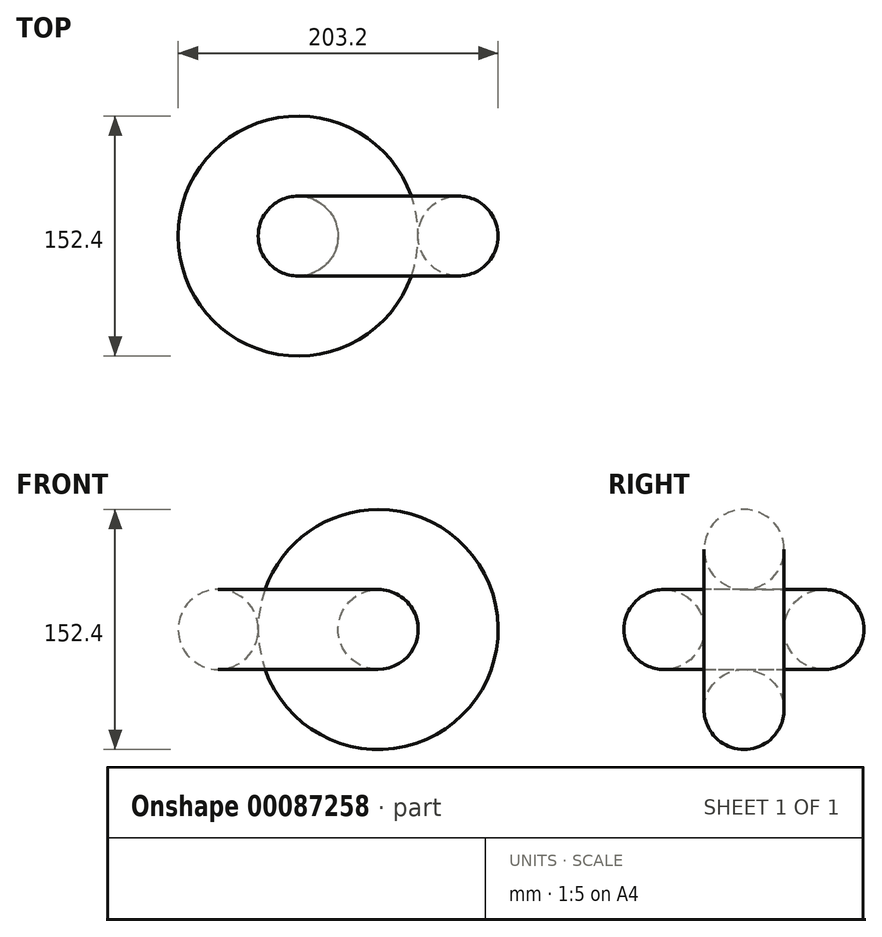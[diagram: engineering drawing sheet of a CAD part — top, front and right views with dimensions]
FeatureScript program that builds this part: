
annotation { "Feature Type Name" : "Feature", "Feature Type Description" : "" }
export const myFeature = defineFeature(function(context is Context, id is Id, definition is map)
    precondition{}
    {
        {
            var Q0;
            Q0=qCreatedBy(makeId("Front.planeOp"),FACE);
            var sketch = newSketch(context, id + "F0", { "sketchPlane" : qUnion([Q0])});
            skCircle(sketch, "E0", {"center": v(-50.8, 0) * mm, "radius": 25.4 * mm});
            skLineSegment(sketch, "E1", {"start": v(0, -55.37) * mm, "end": v(0, 57.8) * mm, "construction": true});
            skSolve(sketch);
        }
        {
            var Q0;
            Q0=makeQuery(id+"F0.imprint","IMPRINT",FACE,{"disambiguationData":[TD([[makeQuery(id+"F0.imprint","IMPRINT",EDGE,{"derivedFrom":sQuery(id+"F0.wireOp",EDGE,"E0")}),1.0]])]});
            var Q1;
            Q1=sQuery(id+"F0.wireOp",EDGE,"E1");
            revolve(context, id + "F1", {"entities" : qUnion([Q0]), "axis" : qUnion([Q1]), "revolveType" : RevolveType.FULL});
        }
        {
            var Q0;
            Q0=qCreatedBy(makeId("Top.planeOp"),FACE);
            var sketch = newSketch(context, id + "F2", { "sketchPlane" : qUnion([Q0])});
            skCircle(sketch, "E2", {"center": v(0, 0) * mm, "radius": 25.4 * mm});
            skLineSegment(sketch, "E3", {"start": v(50.8, 52.34) * mm, "end": v(50.8, -45.36) * mm, "construction": true});
            skSolve(sketch);
        }
        {
            var Q0;
            Q0=makeQuery(id+"F2.imprint","IMPRINT",FACE,{"disambiguationData":[TD([[makeQuery(id+"F2.imprint","IMPRINT",EDGE,{"derivedFrom":sQuery(id+"F2.wireOp",EDGE,"E2")}),1.0]])]});
            var Q1;
            Q1=sQuery(id+"F2.wireOp",EDGE,"E3");
            revolve(context, id + "F3", {"entities" : qUnion([Q0]), "axis" : qUnion([Q1]), "revolveType" : RevolveType.FULL});
        }
    });
